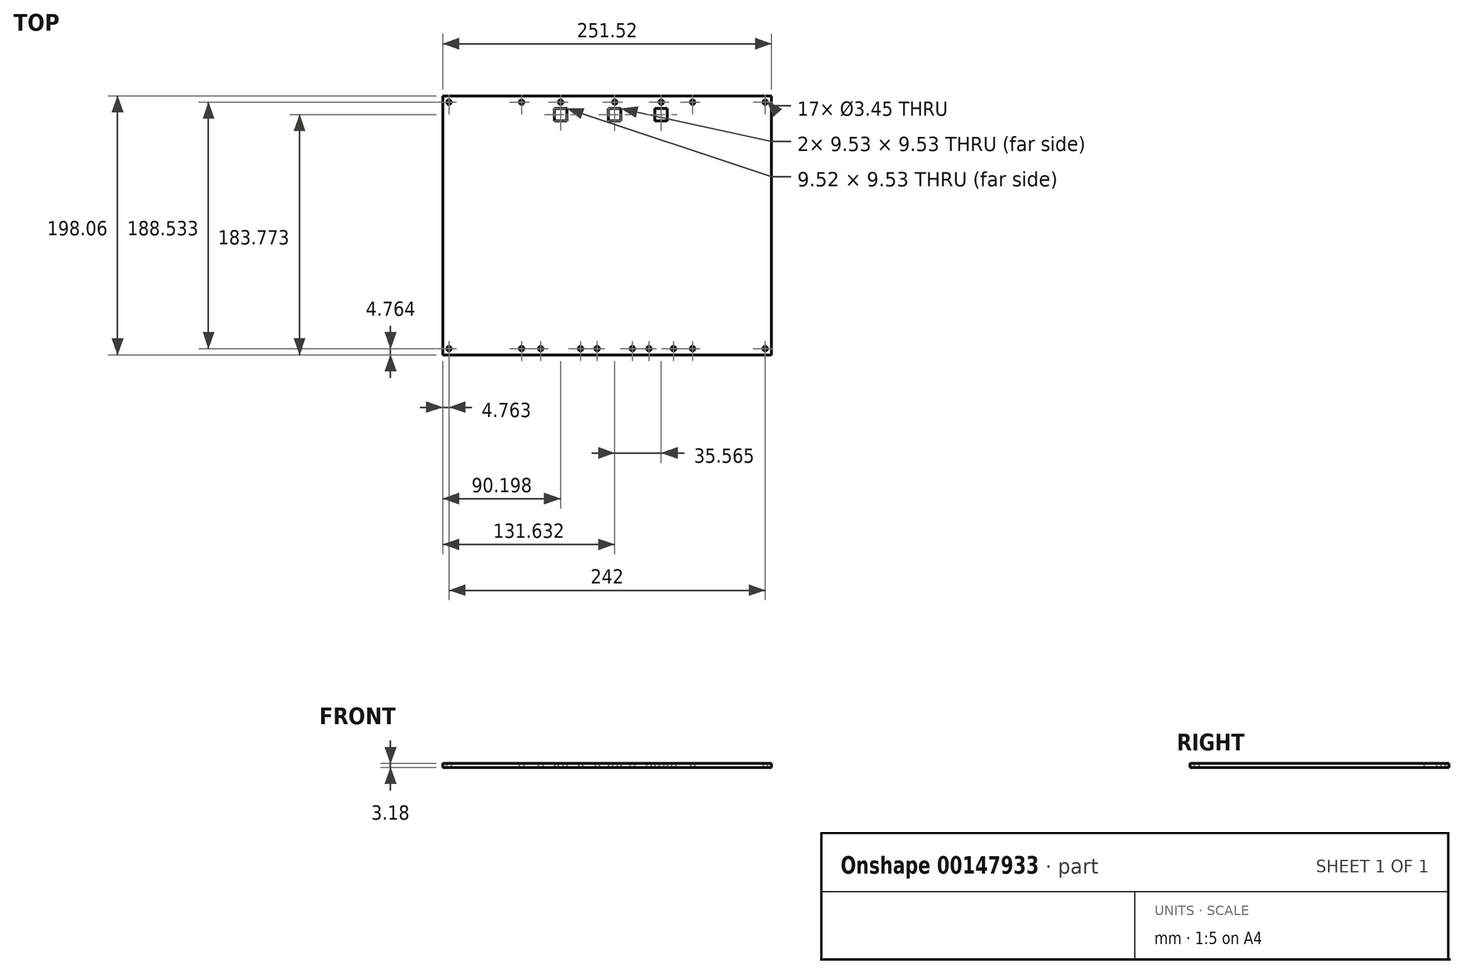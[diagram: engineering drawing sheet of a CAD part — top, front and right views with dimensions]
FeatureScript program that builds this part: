
annotation { "Feature Type Name" : "Feature", "Feature Type Description" : "" }
export const myFeature = defineFeature(function(context is Context, id is Id, definition is map)
    precondition{}
    {
        {
            var Q0;
            Q0=qCreatedBy(makeId("Top.planeOp"),FACE);
            var sketch = newSketch(context, id + "F0", { "sketchPlane" : qUnion([Q0])});
            skLineSegment(sketch, "E0.bottom", {"start": v(0, 0) * mm, "end": v(251.52, 0) * mm});
            skLineSegment(sketch, "E0.top", {"start": v(0, -198.06) * mm, "end": v(251.52, -198.06) * mm});
            skLineSegment(sketch, "E0.left", {"start": v(0, 0) * mm, "end": v(0, -198.06) * mm});
            skLineSegment(sketch, "E0.right", {"start": v(251.52, 0) * mm, "end": v(251.52, -198.06) * mm});
            skLineSegment(sketch, "E1", {"start": v(4.76, 0) * mm, "end": v(4.76, -4.76) * mm, "construction": true});
            skLineSegment(sketch, "E2", {"start": v(4.76, -4.76) * mm, "end": v(0, -4.76) * mm, "construction": true});
            skLineSegment(sketch, "E3", {"start": v(4.76, -4.76) * mm, "end": v(60.33, -4.76) * mm, "construction": true});
            skCircle(sketch, "E4", {"center": v(4.76, -4.76) * mm, "radius": 1.73 * mm});
            skCircle(sketch, "E5", {"center": v(60.33, -4.76) * mm, "radius": 1.73 * mm});
            skLineSegment(sketch, "E6", {"start": v(251.52, -4.76) * mm, "end": v(246.76, -4.76) * mm, "construction": true});
            skLineSegment(sketch, "E7", {"start": v(246.76, -4.76) * mm, "end": v(191.2, -4.76) * mm, "construction": true});
            skLineSegment(sketch, "E8", {"start": v(191.2, -4.76) * mm, "end": v(176.6, -4.76) * mm, "construction": true});
            skCircle(sketch, "E9", {"center": v(191.2, -4.76) * mm, "radius": 1.73 * mm});
            skCircle(sketch, "E10", {"center": v(246.76, -4.76) * mm, "radius": 1.73 * mm});
            skLineSegment(sketch, "E11", {"start": v(4.76, -198.06) * mm, "end": v(4.76, -193.3) * mm, "construction": true});
            skLineSegment(sketch, "E12", {"start": v(4.76, -193.3) * mm, "end": v(60.33, -193.3) * mm, "construction": true});
            skLineSegment(sketch, "E13", {"start": v(176.6, -193.3) * mm, "end": v(191.2, -193.3) * mm, "construction": true});
            skLineSegment(sketch, "E14", {"start": v(191.2, -193.3) * mm, "end": v(246.76, -193.3) * mm, "construction": true});
            skLineSegment(sketch, "E15", {"start": v(246.76, -193.3) * mm, "end": v(251.52, -193.3) * mm, "construction": true});
            skCircle(sketch, "E16", {"center": v(4.76, -193.3) * mm, "radius": 1.73 * mm});
            skCircle(sketch, "E17", {"center": v(60.33, -193.3) * mm, "radius": 1.73 * mm});
            skCircle(sketch, "E18", {"center": v(157.8, -193.3) * mm, "radius": 1.73 * mm});
            skCircle(sketch, "E19", {"center": v(191.2, -193.3) * mm, "radius": 1.73 * mm});
            skCircle(sketch, "E20", {"center": v(176.6, -193.3) * mm, "radius": 1.73 * mm});
            skCircle(sketch, "E21", {"center": v(246.76, -193.3) * mm, "radius": 1.73 * mm});
            skLineSegment(sketch, "E22", {"start": v(60.33, -193.3) * mm, "end": v(74.93, -193.3) * mm, "construction": true});
            skLineSegment(sketch, "E23", {"start": v(74.93, -193.3) * mm, "end": v(105.46, -193.3) * mm, "construction": true});
            skLineSegment(sketch, "E24", {"start": v(60.33, -4.76) * mm, "end": v(74.93, -4.76) * mm, "construction": true});
            skCircle(sketch, "E25", {"center": v(74.93, -193.3) * mm, "radius": 1.73 * mm});
            skCircle(sketch, "E26", {"center": v(105.46, -193.3) * mm, "radius": 1.73 * mm});
            skLineSegment(sketch, "E27", {"start": v(74.93, -4.76) * mm, "end": v(105.46, -4.76) * mm, "construction": true});
            skLineSegment(sketch, "E28", {"start": v(176.6, -193.3) * mm, "end": v(157.8, -193.3) * mm, "construction": true});
            skLineSegment(sketch, "E29", {"start": v(176.6, -4.76) * mm, "end": v(157.8, -4.76) * mm, "construction": true});
            skLineSegment(sketch, "E30", {"start": v(157.8, -193.3) * mm, "end": v(145.1, -193.3) * mm, "construction": true});
            skLineSegment(sketch, "E31", {"start": v(105.46, -193.3) * mm, "end": v(118.16, -193.3) * mm, "construction": true});
            skCircle(sketch, "E32", {"center": v(145.1, -193.3) * mm, "radius": 1.73 * mm});
            skCircle(sketch, "E33", {"center": v(118.16, -193.3) * mm, "radius": 1.73 * mm});
            skLineSegment(sketch, "E34", {"start": v(157.8, -4.76) * mm, "end": v(145.1, -4.76) * mm, "construction": true});
            skLineSegment(sketch, "E35", {"start": v(105.46, -4.76) * mm, "end": v(118.16, -4.76) * mm, "construction": true});
            skLineSegment(sketch, "E36", {"start": v(118.16, -4.76) * mm, "end": v(145.1, -4.76) * mm, "construction": true});
            skCircle(sketch, "E37", {"center": v(90.2, -4.76) * mm, "radius": 1.73 * mm});
            skCircle(sketch, "E38", {"center": v(131.63, -4.76) * mm, "radius": 1.73 * mm});
            skCircle(sketch, "E39", {"center": v(167.2, -4.76) * mm, "radius": 1.73 * mm});
            skLineSegment(sketch, "E40", {"start": v(90.2, -4.76) * mm, "end": v(90.2, -9.53) * mm, "construction": true});
            skLineSegment(sketch, "E41", {"start": v(131.63, -4.76) * mm, "end": v(131.63, -9.52) * mm, "construction": true});
            skLineSegment(sketch, "E42", {"start": v(167.2, -4.76) * mm, "end": v(167.2, -9.52) * mm, "construction": true});
            skLineSegment(sketch, "E43.bottom", {"start": v(85.43, -9.53) * mm, "end": v(94.96, -9.53) * mm});
            skLineSegment(sketch, "E43.top", {"start": v(85.43, -19.05) * mm, "end": v(94.96, -19.05) * mm});
            skLineSegment(sketch, "E43.left", {"start": v(85.43, -9.53) * mm, "end": v(85.43, -19.05) * mm});
            skLineSegment(sketch, "E43.right", {"start": v(94.96, -9.52) * mm, "end": v(94.96, -19.05) * mm});
            skLineSegment(sketch, "E44.bottom", {"start": v(126.87, -9.52) * mm, "end": v(136.4, -9.52) * mm});
            skLineSegment(sketch, "E44.top", {"start": v(126.87, -19.05) * mm, "end": v(136.4, -19.05) * mm});
            skLineSegment(sketch, "E44.left", {"start": v(126.87, -9.52) * mm, "end": v(126.87, -19.05) * mm});
            skLineSegment(sketch, "E44.right", {"start": v(136.4, -9.52) * mm, "end": v(136.4, -19.05) * mm});
            skLineSegment(sketch, "E45.bottom", {"start": v(162.43, -9.52) * mm, "end": v(171.96, -9.52) * mm});
            skLineSegment(sketch, "E45.top", {"start": v(162.43, -19.05) * mm, "end": v(171.96, -19.05) * mm});
            skLineSegment(sketch, "E45.left", {"start": v(162.43, -9.52) * mm, "end": v(162.43, -19.05) * mm});
            skLineSegment(sketch, "E45.right", {"start": v(171.96, -9.52) * mm, "end": v(171.96, -19.05) * mm});
            skSolve(sketch);
        }
        {
            var Q0;
            Q0=qSketchRegion(id+"F0",true);
            extrude(context, id + "F1", {"entities" : qUnion([Q0]), "depth" : 3.17 * mm});
        }
    });
